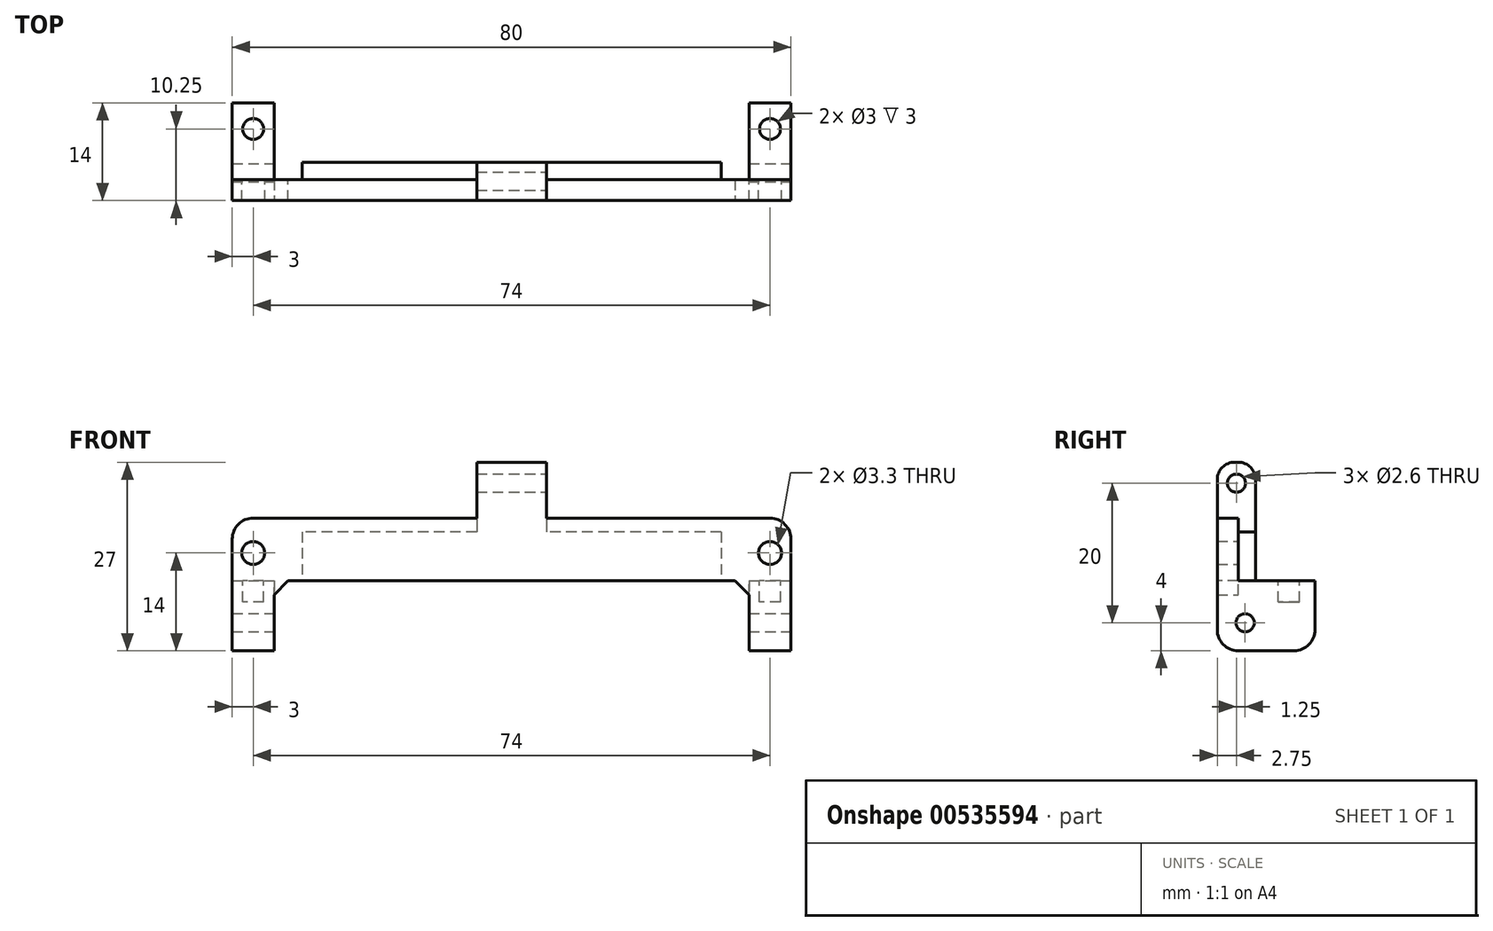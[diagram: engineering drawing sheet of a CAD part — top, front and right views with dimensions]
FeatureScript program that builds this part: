
annotation { "Feature Type Name" : "Feature", "Feature Type Description" : "" }
export const myFeature = defineFeature(function(context is Context, id is Id, definition is map)
    precondition{}
    {
        {
            var Q0;
            Q0=qCreatedBy(makeId("Front.planeOp"),FACE);
            var sketch = newSketch(context, id + "F0", { "sketchPlane" : qUnion([Q0])});
            skLineSegment(sketch, "E0.bottom", {"start": v(34, -4.5) * mm, "end": v(-34, -4.5) * mm});
            skLineSegment(sketch, "E0.top", {"start": v(40, 4.5) * mm, "end": v(-40, 4.5) * mm});
            skLineSegment(sketch, "E0.left", {"start": v(40, -4.5) * mm, "end": v(40, 4.5) * mm});
            skLineSegment(sketch, "E0.right", {"start": v(-40, -4.5) * mm, "end": v(-40, 4.5) * mm});
            skPoint(sketch, "E0.middle", {"position": v(0, 0) * mm});
            skCircle(sketch, "E1", {"center": v(-37, -0.5) * mm, "radius": 1.65 * mm});
            skCircle(sketch, "E2", {"center": v(37, -0.5) * mm, "radius": 1.65 * mm});
            skLineSegment(sketch, "E3", {"start": v(34, -4.5) * mm, "end": v(34, -14.5) * mm});
            skLineSegment(sketch, "E4", {"start": v(34, -14.5) * mm, "end": v(40, -14.5) * mm});
            skLineSegment(sketch, "E5", {"start": v(40, -4.5) * mm, "end": v(40, -14.5) * mm});
            skLineSegment(sketch, "E6", {"start": v(-40, -14.5) * mm, "end": v(-34, -14.5) * mm});
            skLineSegment(sketch, "E7", {"start": v(-34, -14.5) * mm, "end": v(-34, -4.5) * mm});
            skLineSegment(sketch, "E8", {"start": v(-40, -4.5) * mm, "end": v(-40, -14.5) * mm});
            skSolve(sketch);
        }
        {
            var Q0;
            Q0=makeQuery(id+"F0.imprint","IMPRINT",FACE,{"disambiguationData":[TD([[makeQuery(id+"F0.imprint","IMPRINT",EDGE,{"derivedFrom":sQuery(id+"F0.wireOp",EDGE,"E0.bottom")}),-1.0]])]});
            extrude(context, id + "F1", {"entities" : qUnion([Q0]), "depth" : 14 * mm, "offsetDistance" : 25 * mm});
        }
        {
            var Q0;
            Q0=makeQuery(id+"F1.opExtrude","SWEPT_FACE",FACE,{"disambiguationData":[OSD([sQuery(id+"F0.wireOp",EDGE,"E0.left"),sQuery(id+"F0.wireOp",EDGE,"E5")])]});
            var sketch = newSketch(context, id + "F2", { "sketchPlane" : qUnion([Q0])});
            skLineSegment(sketch, "E9", {"start": v(-11, 4.5) * mm, "end": v(-11, -4.5) * mm});
            skLineSegment(sketch, "E10", {"start": v(-11, -4.5) * mm, "end": v(0, -4.5) * mm});
            skLineSegment(sketch, "E11", {"start": v(-11, 4.5) * mm, "end": v(0, 4.5) * mm});
            skLineSegment(sketch, "E12", {"start": v(0, 4.5) * mm, "end": v(0, -4.5) * mm});
            skSolve(sketch);
        }
        {
            var Q0;
            Q0=makeQuery(id+"F2.imprint","IMPRINT",FACE,{"disambiguationData":[TD([[makeQuery(id+"F2.imprint","IMPRINT",EDGE,{"derivedFrom":sQuery(id+"F2.wireOp",EDGE,"E9")}),1.0]])]});
            extrude(context, id + "F3", {"entities" : qUnion([Q0]), "operationType" : NewBodyOperationType.REMOVE, "endBound" : BoundingType.THROUGH_ALL, "oppositeDirection" : true, "depth" : 25 * mm, "offsetDistance" : 25 * mm});
        }
        {
            var Q0;
            Q0=makeQuery(id+"F1.opExtrude","SWEPT_FACE",FACE,{"disambiguationData":[OSD([sQuery(id+"F0.wireOp",EDGE,"E0.left"),sQuery(id+"F0.wireOp",EDGE,"E5")])]});
            var sketch = newSketch(context, id + "F4", { "sketchPlane" : qUnion([Q0])});
            skCircle(sketch, "E13", {"center": v(-10, -10.5) * mm, "radius": 1.3 * mm});
            skCircle(sketch, "E14", {"center": v(-10, -10.5) * mm, "radius": 4 * mm});
            skCircle(sketch, "E15", {"center": v(-2.44, -10.5) * mm, "radius": 4 * mm});
            skSolve(sketch);
        }
        {
            var Q0;
            Q0=makeQuery(id+"F4.imprint","IMPRINT",FACE,{"disambiguationData":[TD([[makeQuery(id+"F4.imprint","IMPRINT",EDGE,{"derivedFrom":sQuery(id+"F4.wireOp",EDGE,"E13")}),1.0]])]});
            extrude(context, id + "F5", {"entities" : qUnion([Q0]), "operationType" : NewBodyOperationType.REMOVE, "endBound" : BoundingType.THROUGH_ALL, "oppositeDirection" : true, "depth" : 25 * mm, "offsetDistance" : 25 * mm});
        }
        {
            var Q0;
            Q0=makeQuery(id+"F1.opExtrude","CAP_EDGE",EDGE,{"disambiguationData":[OSD([sQuery(id+"F0.wireOp",EDGE,"E4")])],"isStart":false});
            var Q1;
            Q1=makeQuery(id+"F1.opExtrude","CAP_EDGE",EDGE,{"disambiguationData":[OSD([sQuery(id+"F0.wireOp",EDGE,"E6")])],"isStart":false});
            var Q2;
            Q2=makeQuery(id+"F1.opExtrude","CAP_EDGE",EDGE,{"disambiguationData":[OSD([sQuery(id+"F0.wireOp",EDGE,"E6")])],"isStart":true});
            var Q3;
            Q3=makeQuery(id+"F1.opExtrude","CAP_EDGE",EDGE,{"disambiguationData":[OSD([sQuery(id+"F0.wireOp",EDGE,"E4")])],"isStart":true});
            var Q4;
            Q4=makeQuery(id+"F1.opExtrude","SWEPT_EDGE",EDGE,{"disambiguationData":[OSD([sQuery(id+"F0.wireOp",EDGE,"E0.top"),sQuery(id+"F0.wireOp",EDGE,"E0.left")])]});
            var Q5;
            Q5=makeQuery(id+"F1.opExtrude","SWEPT_EDGE",EDGE,{"disambiguationData":[OSD([sQuery(id+"F0.wireOp",EDGE,"E0.top"),sQuery(id+"F0.wireOp",EDGE,"E0.right")])]});
            fillet(context, id + "F6", {"entities" : qUnion([Q0, Q1, Q2, Q3, Q4, Q5]), "radius" : 3 * mm, "tangentPropagation" : true, "allowEdgeOverflow" : false});
        }
        {
            var Q0;
            {var subQ0=sQuery(id+"F0.wireOp",EDGE,"E0.bottom");var subQ1=sQuery(id+"F0.wireOp",EDGE,"E3");Q0=makeQuery(id+"F3.boolean.opBoolean","SPLIT",EDGE,{"disambiguationData":[topologyDisambiguationEdgeConnected([makeQuery(id+"F1.opExtrude","SWEPT_FACE",FACE,{"disambiguationData":[OSD([subQ0])]})])],"derivedFrom":makeQuery(id+"F1.opExtrude","SWEPT_EDGE",EDGE,{"disambiguationData":[OSD([subQ0,subQ1])]})});}
            var Q1;
            {var subQ0=sQuery(id+"F0.wireOp",EDGE,"E0.bottom");var subQ1=sQuery(id+"F0.wireOp",EDGE,"E7");Q1=makeQuery(id+"F3.boolean.opBoolean","SPLIT",EDGE,{"disambiguationData":[topologyDisambiguationEdgeConnected([makeQuery(id+"F1.opExtrude","SWEPT_FACE",FACE,{"disambiguationData":[OSD([subQ0])]})])],"derivedFrom":makeQuery(id+"F1.opExtrude","SWEPT_EDGE",EDGE,{"disambiguationData":[OSD([subQ0,subQ1])]})});}
            chamfer(context, id + "F7", {"entities" : qUnion([Q0, Q1]), "width" : 2 * mm, "tangentPropagation" : true});
        }
        {
            var Q0;
            {var subQ0=sQuery(id+"F0.wireOp",EDGE,"E3");Q0=makeQuery(id+"F3.boolean.opBoolean","COPY",FACE,{"disambiguationData":[TD([makeQuery(id+"F1.opExtrude","SWEPT_FACE",FACE,{"disambiguationData":[OSD([subQ0])]})])],"derivedFrom":makeQuery(id+"F3.opExtrude","SWEPT_FACE",FACE,{"disambiguationData":[OSD([sQuery(id+"F2.wireOp",EDGE,"E10")])]})});}
            var sketch = newSketch(context, id + "F8", { "sketchPlane" : qUnion([Q0])});
            skCircle(sketch, "E16", {"center": v(-37, -3.75) * mm, "radius": 1.5 * mm});
            skCircle(sketch, "E17", {"center": v(37, -3.75) * mm, "radius": 1.5 * mm});
            skSolve(sketch);
        }
        {
            var Q0;
            Q0=makeQuery(id+"F8.imprint","IMPRINT",FACE,{"disambiguationData":[TD([[makeQuery(id+"F8.imprint","IMPRINT",EDGE,{"derivedFrom":sQuery(id+"F8.wireOp",EDGE,"E16")}),1.0]])]});
            var Q1;
            Q1=makeQuery(id+"F8.imprint","IMPRINT",FACE,{"disambiguationData":[TD([[makeQuery(id+"F8.imprint","IMPRINT",EDGE,{"derivedFrom":sQuery(id+"F8.wireOp",EDGE,"E17")}),1.0]])]});
            extrude(context, id + "F9", {"entities" : qUnion([Q0, Q1]), "operationType" : NewBodyOperationType.REMOVE, "oppositeDirection" : true, "depth" : 3 * mm, "offsetDistance" : 25 * mm});
        }
        {
            var Q0;
            Q0=makeQuery(id+"F3.boolean.opBoolean","COPY",FACE,{"derivedFrom":makeQuery(id+"F3.opExtrude","SWEPT_FACE",FACE,{"disambiguationData":[OSD([sQuery(id+"F2.wireOp",EDGE,"E9")])]})});
            var sketch = newSketch(context, id + "F10", { "sketchPlane" : qUnion([Q0])});
            skLineSegment(sketch, "E18.bottom", {"start": v(-30, 2.5) * mm, "end": v(-5, 2.5) * mm});
            skLineSegment(sketch, "E18.top", {"start": v(-30, -4.5) * mm, "end": v(30, -4.5) * mm});
            skLineSegment(sketch, "E18.left", {"start": v(-30, 2.5) * mm, "end": v(-30, -4.5) * mm});
            skLineSegment(sketch, "E18.right", {"start": v(30, 2.5) * mm, "end": v(30, -4.5) * mm});
            skLineSegment(sketch, "E19.bottom", {"start": v(-5, 10.5) * mm, "end": v(5, 10.5) * mm});
            skLineSegment(sketch, "E19.left", {"start": v(-5, 10.5) * mm, "end": v(-5, 2.5) * mm});
            skLineSegment(sketch, "E19.right", {"start": v(5, 10.5) * mm, "end": v(5, 2.5) * mm});
            skLineSegment(sketch, "E20.trimOffspring", {"start": v(5, 2.5) * mm, "end": v(30, 2.5) * mm});
            skSolve(sketch);
        }
        {
            var Q0;
            {var subQ5=sQuery(id+"F10.wireOp",EDGE,"E18.bottom");Q0=makeQuery(id+"F10.imprint","IMPRINT",FACE,{"disambiguationData":[TD([[makeQuery(id+"F10.imprint","IMPRINT",EDGE,{"derivedFrom":subQ5}),-1.0]])]});}
            extrude(context, id + "F11", {"entities" : qUnion([Q0]), "operationType" : NewBodyOperationType.ADD, "depth" : 2.5 * mm, "offsetDistance" : 25 * mm});
        }
        {
            var Q0;
            Q0=makeQuery(id+"F11.opExtrude","CAP_FACE",FACE,{"disambiguationData":[OSD([sQuery(id+"F0.wireOp",EDGE,"E0.top"),sQuery(id+"F0.wireOp",EDGE,"E0.left"),sQuery(id+"F2.wireOp",EDGE,"E9"),sQuery(id+"F2.wireOp",EDGE,"E11"),sQuery(id+"F10.wireOp",EDGE,"E18.bottom"),sQuery(id+"F10.wireOp",EDGE,"E18.top"),sQuery(id+"F10.wireOp",EDGE,"E18.left"),sQuery(id+"F10.wireOp",EDGE,"E18.right"),sQuery(id+"F10.wireOp",EDGE,"E19.left"),sQuery(id+"F10.wireOp",EDGE,"E19.right"),sQuery(id+"F10.wireOp",EDGE,"E20.trimOffspring")])],"isStart":false});
            var sketch = newSketch(context, id + "F12", { "sketchPlane" : qUnion([Q0])});
            skLineSegment(sketch, "E21", {"start": v(-5, 2.5) * mm, "end": v(-5, 12.5) * mm});
            skPoint(sketch, "E21.endSnap0", {"position": v(-5, 3.5) * mm});
            skLineSegment(sketch, "E22", {"start": v(-5, 12.5) * mm, "end": v(5, 12.5) * mm});
            skLineSegment(sketch, "E23", {"start": v(5, 12.5) * mm, "end": v(5, 2.5) * mm});
            skLineSegment(sketch, "E24", {"start": v(5, 2.5) * mm, "end": v(-5, 2.5) * mm});
            skSolve(sketch);
        }
        {
            var Q0;
            {var subQ2=sQuery(id+"F12.wireOp",EDGE,"E22");Q0=makeQuery(id+"F12.imprint","IMPRINT",FACE,{"disambiguationData":[TD([[makeQuery(id+"F12.imprint","IMPRINT",EDGE,{"derivedFrom":subQ2}),-1.0]])]});}
            var Q1;
            {var subQ0=sQuery(id+"F12.wireOp",EDGE,"E24");Q1=makeQuery(id+"F12.imprint","IMPRINT",FACE,{"disambiguationData":[TD([[makeQuery(id+"F12.imprint","IMPRINT",EDGE,{"derivedFrom":subQ0}),-1.0]])]});}
            extrude(context, id + "F13", {"entities" : qUnion([Q0, Q1]), "operationType" : NewBodyOperationType.ADD, "oppositeDirection" : true, "depth" : 5.5 * mm, "offsetDistance" : 25 * mm});
        }
        {
            var Q0;
            Q0=makeQuery(id+"F13.opExtrude","CAP_EDGE",EDGE,{"disambiguationData":[OSD([sQuery(id+"F12.wireOp",EDGE,"E22")])],"isStart":false});
            var Q1;
            Q1=makeQuery(id+"F13.opExtrude","CAP_EDGE",EDGE,{"disambiguationData":[OSD([sQuery(id+"F12.wireOp",EDGE,"E22")])],"isStart":true});
            fillet(context, id + "F14", {"entities" : qUnion([Q0, Q1]), "radius" : 2.5 * mm, "tangentPropagation" : true, "allowEdgeOverflow" : false});
        }
        {
            var Q0;
            Q0=makeQuery(id+"F13.boolean.opBoolean","MERGE",FACE,{"derivedFrom":[makeQuery(id+"F11.opExtrude","SWEPT_FACE",FACE,{"disambiguationData":[OSD([sQuery(id+"F10.wireOp",EDGE,"E19.left")])]}),makeQuery(id+"F13.opExtrude","SWEPT_FACE",FACE,{"disambiguationData":[OSD([sQuery(id+"F12.wireOp",EDGE,"E21")])]})]});
            var sketch = newSketch(context, id + "F15", { "sketchPlane" : qUnion([Q0])});
            skCircle(sketch, "E25", {"center": v(-11.25, 9.5) * mm, "radius": 1.3 * mm});
            skSolve(sketch);
        }
        {
            var Q0;
            Q0=makeQuery(id+"F15.imprint","IMPRINT",FACE,{"disambiguationData":[TD([[makeQuery(id+"F15.imprint","IMPRINT",EDGE,{"derivedFrom":sQuery(id+"F15.wireOp",EDGE,"E25")}),1.0]])]});
            extrude(context, id + "F16", {"entities" : qUnion([Q0]), "operationType" : NewBodyOperationType.REMOVE, "endBound" : BoundingType.THROUGH_ALL, "oppositeDirection" : true, "depth" : 25 * mm, "offsetDistance" : 25 * mm});
        }
    });
